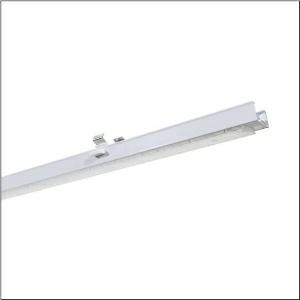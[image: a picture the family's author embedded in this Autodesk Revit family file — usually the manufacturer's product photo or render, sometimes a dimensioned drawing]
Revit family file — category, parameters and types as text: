
# Revit family: trunking_flex_31_51re18ma46b
name_source: partatom
category: Lighting Fixtures
units: mm (PartAtom-declared; Revit-internal decimal feet)

## family parameters
Cut with Voids When Loaded = No
Host = Face
Light Source = No
Part Type = Normal
Room Calculation Point = No
Round Connector Dimension = Use Diameter
Shared = No

## types (1)
- --- (1 x LED, 6400 lm, 40 W, 4000K)
    Apparent Load = 40 VA
    CIE Flux Codes = 71 89 97 97 100
    Color Rendering = 80
    Color Temperature = 4000K
    Default Elevation = 1800 mm
    Description = Trunking Flex 31, luminaire insert, of extruded aluminium section, coated, traffic white (RAL 9016), length: 1.172mm, width: 91mm, height: 53mm, LED rated luminous flux: 6.400lm, light colour: 840, control gear: ON/OFF Multilumen, with system connector: socket, mains connection: 220..240V, AC, 50/60Hz, rated input power: 40W, luminous flux adjustable on luminaire in four steps (3420/4540/5580/6630lm), connected load according to luminous flux setting (20/26/33/40W), primary light control with lens, of plastic, primary optical cover: cover, of PMMA, light emission: direct distribution, protection rating (complete): IP20, insulation class (complete): insulation class I (protective earthing), certification: CE, UKCA, impact resistance: IK02, permissible ambient temperature for indoor applications: -20..+40°C, packaging unit: 1 piece
    Height = 58 mm
    Lamp = 1 x LED
    Lamp Light Flux = 6400 lm
    Lamp Power = 40 W
    Lamp count = 1
    Length = 1172 mm
    Luminous efficacy = 160 lm/W
    Manufacturer = Siteco
    ModVariant = No
    Model = 51RE18MA46B
    Mounting Place = Ceiling
    Mounting Type = Pendant
    Number of Poles = 1
    OnlyDefault = Yes
    Power Factor = 1
    Product Name = Trunking Flex 31
    Product group = luminaire insert
    ProductGroupID = 902
    Protection Class = Protection class I
    Protection Degree = IP 20
    RLX_Detail_Level = 1
    RLX_Emergency_Light_Flux = 0 lm
    RLX_Emergency_Type = 0
    RLX_Emergency_Type_DB = No
    RlxData = <blob elided: 20057 chars, md5=55b54b06>
    Socket = socket
    Standby Power = 0 W
    System Light Flux = 6400 lm
    System Power = 40 W
    Type Comments = factory setting: luminous flux: 100 % | (ON | ON) | 300 mA
    Type Image = l_1266702.jpg
    URL = http://relux.com
    VarID = @adj_059102
    Voltage = 0 V
    Weight = 0.00 kg
    Width = 65 mm

## geometry (parser evidence)
native form markers: Blend x4, Sweep x11
no freeform markers — native parametric forms only
